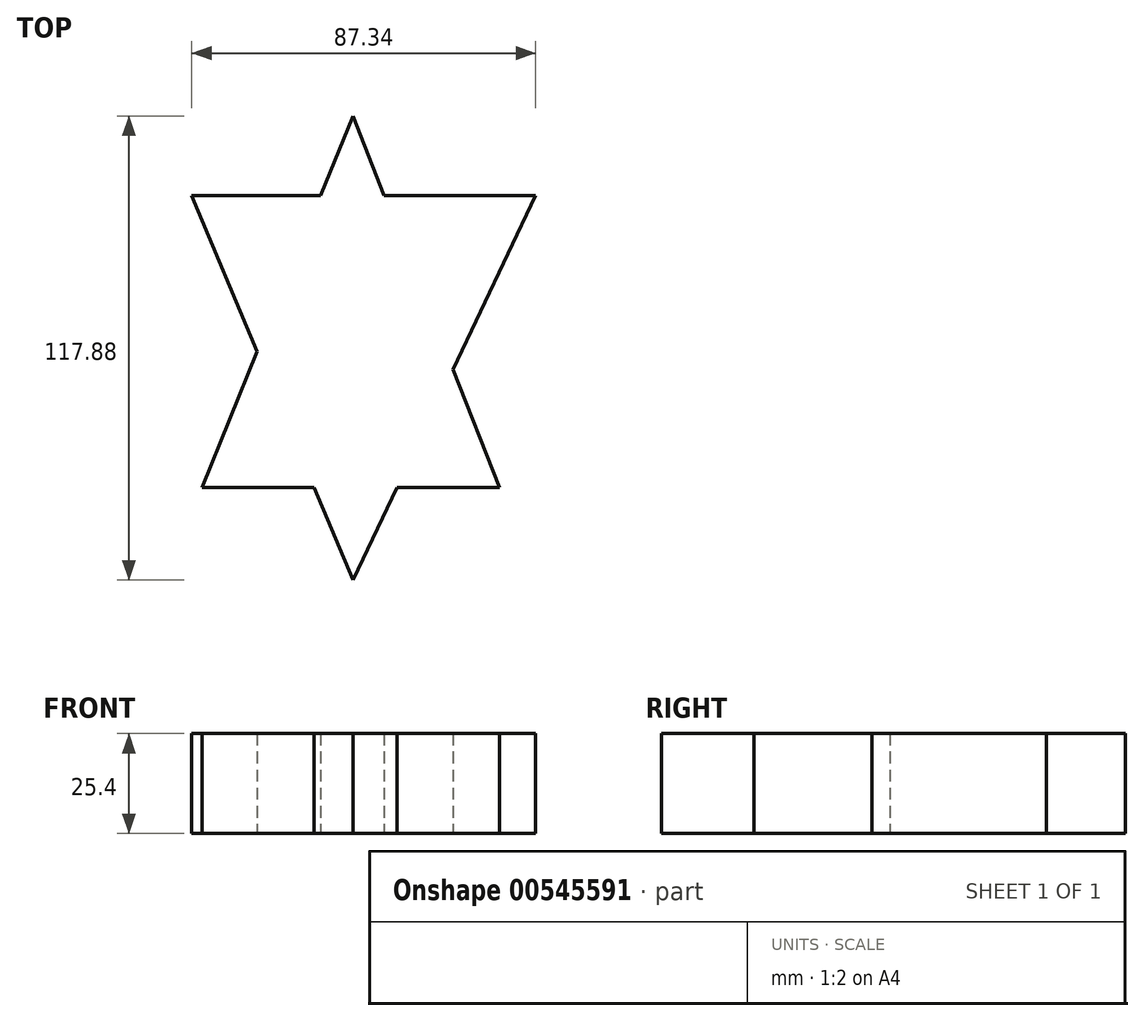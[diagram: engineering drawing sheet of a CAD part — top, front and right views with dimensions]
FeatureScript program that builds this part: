
annotation { "Feature Type Name" : "Feature", "Feature Type Description" : "" }
export const myFeature = defineFeature(function(context is Context, id is Id, definition is map)
    precondition{}
    {
        {
            var Q0;
            Q0=qCreatedBy(makeId("Top.planeOp"),FACE);
            var sketch = newSketch(context, id + "F0", { "sketchPlane" : qUnion([Q0])});
            skLineSegment(sketch, "E0", {"start": v(-40.92, 29.32) * mm, "end": v(46.42, 29.32) * mm});
            skLineSegment(sketch, "E1", {"start": v(-40.92, 29.32) * mm, "end": v(0, -68.4) * mm});
            skLineSegment(sketch, "E2", {"start": v(0, -68.4) * mm, "end": v(46.42, 29.32) * mm});
            skLineSegment(sketch, "E3", {"start": v(37.56, -44.9) * mm, "end": v(-38.33, -44.9) * mm});
            skLineSegment(sketch, "E4", {"start": v(-38.33, -44.9) * mm, "end": v(0, 49.47) * mm});
            skLineSegment(sketch, "E5", {"start": v(0, 49.47) * mm, "end": v(37.56, -45.8) * mm});
            skSolve(sketch);
        }
        {
            var Q0;
            Q0 = qSketchRegion(id + "F0", true);
            extrude(context, id + "F1", {"entities" : qUnion([Q0]), "depth" : 25.4 * mm, "offsetDistance" : 25.4 * mm});
        }
    });
